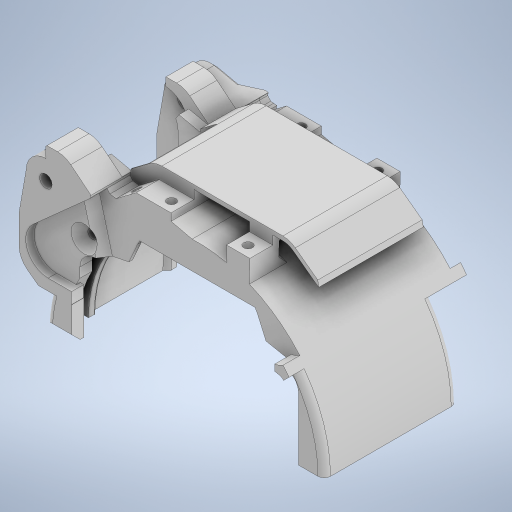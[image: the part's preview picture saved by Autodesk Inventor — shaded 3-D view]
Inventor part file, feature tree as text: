
AUTODESK INVENTOR PART (.ipt)
format: ipt  version: 2023.4 (Build 274418000, 418)  size: 2,114,560 bytes
history: native  units: mm
features: extrude x63, sketch x63, projected_geometry x51, chamfer x16, thicken_offset x6, fillet x4, plane x3
ambient origin geometry x8: Origin, YZ Plane, XZ Plane, XY Plane, X Axis, Y Axis, Z Axis, Center Point
bodies: Solid1 (feature_tree)
feature tree (206):
  extrude  "Extrusion1"  Depth=2.0mm
  extrude  "Extrusion2"  Depth=122.0mm
  extrude  "Extrusion3"  Depth=4.6mm TaperAngle=0.0deg
  extrude  "Extrusion4"  Depth=2.0mm TaperAngle=0.0deg
  extrude  "Extrusion5"  Depth=0.1mm
  thicken_offset  "Thicken1"
  thicken_offset  "Thicken2"
  extrude  "Extrusion6"  Depth=0.1mm
  extrude  "Extrusion7"  Depth=7.0mm TaperAngle=0.0deg
  extrude  "Extrusion8"  Depth=10.0mm TaperAngle=0.0deg
  extrude  "Extrusion9"  Depth=9.0mm TaperAngle=0.0deg
  extrude  "Extrusion10"  Depth=10.0mm TaperAngle=0.0deg
  extrude  "Extrusion11"  Depth=15.0mm TaperAngle=0.0deg
  extrude  "Extrusion12"  Depth=3.0mm
  sketch  "Sketch13"  dims[d40=4.0mm d41=0.0mm d42=12.0mm d43=0.0mm]
  plane  "Work Plane1"
  extrude  "Extrusion13"  Depth=12.0mm TaperAngle=0.0deg
  extrude  "Extrusion14"  Depth=7.0mm TaperAngle=0.0deg
  extrude  "Extrusion15"  Depth=5.0mm TaperAngle=0.0deg
  extrude  "Extrusion16"  Depth=1.0mm TaperAngle=0.0deg
  extrude  "Extrusion17"  Depth=4.0mm TaperAngle=0.0deg
  extrude  "Extrusion18"  Depth=10.0mm TaperAngle=0.0deg
  extrude  "Extrusion19"  Depth=15.0mm TaperAngle=0.0deg
  extrude  "Extrusion20"  Depth=10.0mm TaperAngle=0.0deg
  extrude  "Extrusion21"  Depth=1.3mm TaperAngle=45.0deg
  extrude  "Extrusion22"  Depth=10.0mm TaperAngle=0.0deg
  extrude  "Extrusion23"  Depth=3.0mm TaperAngle=0.0deg
  extrude  "Extrusion24"  Depth=2.0mm TaperAngle=45.0deg
  extrude  "Extrusion25"  Depth=3.0mm TaperAngle=0.0deg
  extrude  "Extrusion28"  Depth=10.0mm
  extrude  "Extrusion29"  Depth=4.0mm TaperAngle=45.0deg
  fillet  "Fillet2"  Radius=4.0mm
  extrude  "Extrusion30"  Depth=4.25mm
  extrude  "Extrusion31"  Depth=4.25mm
  extrude  "Extrusion32"  Depth=4.25mm
  chamfer  "Chamfer4"  Distance=9.0mm
  chamfer  "Chamfer5"  Distance=9.0mm
  chamfer  "Chamfer6"  Distance=6.0mm
  extrude  "Extrusion33"  Depth=6.0mm TaperAngle=0.0deg
  extrude  "Extrusion34"  Depth=4.0mm TaperAngle=0.0deg
  extrude  "Extrusion35"  Depth=30.0mm
  chamfer  "Chamfer7"  Distance=32.5mm
  extrude  "Extrusion36"  Depth=10.0mm
  extrude  "Extrusion37"  Depth=3.0mm TaperAngle=0.0deg
  extrude  "Extrusion38"  Depth=2.0mm TaperAngle=0.0deg
  chamfer  "Chamfer8"  Distance=4.0mm Angle=45.0deg
  chamfer  "Chamfer9"  Distance=4.0mm Angle=45.0deg
  chamfer  "Chamfer10"  Distance=0.5mm Angle=45.0deg
  extrude  "Extrusion39"  Depth=10.0mm
  extrude  "Extrusion40"  Depth=0.2mm
  extrude  "Extrusion41"  Depth=0.2mm
  extrude  "Extrusion42"  Depth=3.0mm TaperAngle=0.0deg
  extrude  "Extrusion43"  Depth=4.0mm TaperAngle=45.0deg
  extrude  "Extrusion44"  Depth=4.5mm
  extrude  "Extrusion45"  Depth=2.5mm
  extrude  "Extrusion46"  Depth=10.0mm TaperAngle=45.0deg
  extrude  "Extrusion47"  Depth=10.0mm TaperAngle=0.0deg
  plane  "Work Plane2"
  extrude  "Extrusion48"  Depth=10.0mm TaperAngle=0.0deg
  extrude  "Extrusion50"  Depth=4.0mm TaperAngle=45.0deg
  thicken_offset  "Thicken3"
  extrude  "Extrusion52"  Depth=3.0mm
  extrude  "Extrusion53"  TaperAngle=0.0deg  [1 undecoded]
  extrude  "Extrusion54"  Depth=2.0mm
  chamfer  "Chamfer13"  Distance=44.0mm
  chamfer  "Chamfer14"  Distance=4.0mm Angle=45.0deg
  chamfer  "Chamfer15"  Distance=44.0mm
  fillet  "Fillet3"  Radius=0.5mm
  thicken_offset  "Thicken4"
  thicken_offset  "Thicken5"
  thicken_offset  "Thicken6"
  extrude  "Extrusion55"  [1 undecoded]
  extrude  "Extrusion56"  [1 undecoded]
  extrude  "Extrusion57"  [1 undecoded]
  chamfer  "Chamfer16"  [1 undecoded]
  chamfer  "Chamfer18"  [1 undecoded]
  extrude  "Extrusion58"  [1 undecoded]
  extrude  "Extrusion59"  [1 undecoded]
  chamfer  "Chamfer19"  [1 undecoded]
  extrude  "Extrusion60"  [1 undecoded]
  extrude  "Extrusion61"  [1 undecoded]
  extrude  "Extrusion62"  [1 undecoded]
  extrude  "Extrusion63"  [1 undecoded]
  chamfer  "Chamfer21"  [1 undecoded]
  chamfer  "Chamfer22"  [1 undecoded]
  fillet  "Fillet4"  [1 undecoded]
  fillet  "Fillet5"  [1 undecoded]
  extrude  "Extrusion64"  [1 undecoded]
  extrude  "Extrusion65"  [1 undecoded]
  plane  "Work Plane3"
  extrude  "Extrusion66"  [1 undecoded]
  chamfer  "Chamfer23"  [1 undecoded]
  extrude  "Extrusion67"  [1 undecoded]
  sketch  "Sketch1"  dims[d0=125.0mm d1=2.0mm]
  sketch  "Sketch2"  dims[d2=4.6mm d3=0.0mm d4=122.0mm]
  sketch  "Sketch3"  dims[d5=42.8mm d6=0.0mm d7=4.6mm d8=0.0mm]
  projected_geometry  "Projected Loop1"
  sketch  "Sketch4"  dims[d10=2.0mm d11=0.0mm d12=2.0mm d13=0.0mm]
  sketch  "Sketch5"  dims[d14=0.1mm d15=0.1mm]
  projected_geometry  "Projected Loop2"
  projected_geometry  "Projected Loop3"
  sketch  "Sketch6"  dims[d16=0.1mm d17=0.1mm]
  projected_geometry  "Projected Loop4"
  sketch  "Sketch7"  dims[d18=0.0mm d19=0.0mm d20=7.0mm d21=0.0mm]
  projected_geometry  "Projected Loop5"
  sketch  "Sketch8"  dims[d22=0.0mm d23=0.0mm d24=10.0mm d25=0.0mm]
  projected_geometry  "Projected Loop6"
  projected_geometry  "Projected Loop7"
  sketch  "Sketch9"  dims[d26=9.0mm d27=0.0mm d28=9.0mm d29=0.0mm]
  projected_geometry  "Projected Loop8"
  sketch  "Sketch10"  dims[d30=10.0mm d31=0.0mm d32=10.0mm d33=0.0mm]
  sketch  "Sketch11"  dims[d34=15.0mm d35=0.0mm d36=15.0mm d37=0.0mm]
  projected_geometry  "Projected Loop9"
  sketch  "Sketch12"  dims[d38=3.0mm d39=3.0mm]
  projected_geometry  "Projected Loop10"
  sketch  "Sketch14"  dims[d44=3.0mm d45=0.0mm d46=7.0mm d47=0.0mm]
  projected_geometry  "Projected Loop11"
  projected_geometry  "Projected Loop12"
  sketch  "Sketch15"  dims[d48=2.0mm d49=0.0mm d50=5.0mm d51=0.0mm]
  sketch  "Sketch16"  dims[d52=5.0mm d53=0.0mm d54=1.0mm d55=0.0mm]
  projected_geometry  "Projected Loop13"
  sketch  "Sketch17"  dims[d56=4.0mm d57=0.0mm d58=4.0mm d59=0.0mm]
  sketch  "Sketch18"  dims[d74=10.0mm d75=0.0mm d76=3.9mm d77=0.0mm]
  projected_geometry  "Projected Loop14"
  sketch  "Sketch19"  dims[d78=3.0mm d79=15.0mm d80=0.0mm]
  sketch  "Sketch20"  dims[d81=15.0mm d82=0.0mm d83=10.0mm d84=0.0mm]
  projected_geometry  "Projected Loop15"
  sketch  "Sketch21"  dims[d85=4.0mm d86=2.0mm d87=45.0deg d88=1.3mm d89=2.0mm d90=45.0deg]
  projected_geometry  "Projected Loop16"
  sketch  "Sketch22"  dims[d91=3.0mm d92=2.0mm d93=45.0deg d94=10.0mm d95=0.0mm]
  projected_geometry  "Projected Loop17"
  projected_geometry  "Projected Loop18"
  projected_geometry  "Projected Loop19"
  projected_geometry  "Projected Loop20"
  projected_geometry  "Projected Loop21"
  projected_geometry  "Projected Loop22"
  projected_geometry  "Projected Loop23"
  projected_geometry  "Projected Loop24"
  projected_geometry  "Projected Loop25"
  projected_geometry  "Projected Loop26"
  sketch  "Sketch24"  dims[d96=2.0mm d97=3.0mm d98=0.0mm]
  projected_geometry  "Projected Loop28"
  sketch  "Sketch25"  dims[d99=3.0mm d100=0.0mm d101=2.0mm d102=2.0mm d103=45.0deg]
  sketch  "Sketch26"  dims[d104=6.0mm d105=3.0mm d106=0.0mm]
  sketch  "Sketch29"  dims[d107=10.0mm d108=0.0mm d109=11.2mm]
  projected_geometry  "Projected Loop31"
  sketch  "Sketch30"  dims[d110=6.0mm d111=0.0mm d112=4.0mm d113=2.0mm d114=45.0deg]
  projected_geometry  "Projected Loop32"
  sketch  "Sketch31"  dims[d115=2.0mm d116=2.0mm d117=45.0deg]
  sketch  "Sketch32"  dims[d118=1.0mm d119=2.0mm d120=45.0deg d121=4.0mm d122=0.0mm]
  sketch  "Sketch33"  dims[d123=4.25mm d124=4.25mm]
  sketch  "Sketch34"  dims[d125=4.25mm d126=4.25mm]
  sketch  "Sketch35"  dims[d127=9.0mm d128=0.0mm d129=4.25mm]
  sketch  "Sketch36"  dims[d130=4.25mm d131=9.0mm d132=0.0mm]
  projected_geometry  "Projected Loop33"
  sketch  "Sketch37"  dims[d133=4.25mm]
  projected_geometry  "Projected Loop34"
  sketch  "Sketch38"  dims[d134=4.25mm d135=9.0mm d136=0.0mm d137=6.0mm d138=0.0mm]
  projected_geometry  "Projected Loop35"
  sketch  "Sketch39"  dims[d139=6.0mm d140=0.0mm d141=6.0mm d142=0.0mm]
  sketch  "Sketch40"  dims[d143=9.0mm d144=0.0mm d145=4.0mm d146=0.0mm]
  projected_geometry  "Projected Loop36"
  sketch  "Sketch41"  dims[d147=-5.0mm d148=30.0mm d149=32.5mm d150=0.0mm]
  sketch  "Sketch42"  dims[d153=10.0mm d154=0.0mm d163=0.2mm]
  sketch  "Sketch43"  dims[d164=0.2mm d165=3.0mm d166=0.0mm]
  sketch  "Sketch44"  dims[d167=2.0mm d168=0.0mm d169=2.0mm d170=0.0mm d171=4.0mm d172=2.0mm d173=45.0deg d174=4.0mm d175=2.0mm d176=45.0deg d177=0.5mm d178=2.0mm d179=45.0deg]
  sketch  "Sketch45"  dims[d180=10.0mm d181=0.2mm]
  projected_geometry  "Projected Loop37"
  sketch  "Sketch46"  dims[d182=0.2mm d183=0.2mm d184=0.2mm]
  projected_geometry  "Projected Loop38"
  sketch  "Sketch47"  dims[d185=0.2mm d186=0.2mm]
  projected_geometry  "Projected Loop39"
  sketch  "Sketch48"  dims[d187=3.0mm d188=0.0mm d189=3.0mm d190=0.0mm]
  projected_geometry  "Projected Loop40"
  sketch  "Sketch49"  dims[d191=5.0mm d192=0.0mm d193=4.0mm d194=2.0mm d195=45.0deg]
  sketch  "Sketch51"  dims[d199=4.0mm d200=2.0mm d201=45.0deg d202=4.5mm]
  projected_geometry  "Projected Loop41"
  sketch  "Sketch53"  dims[d203=0.0mm d204=0.0mm d205=2.5mm]
  projected_geometry  "Projected Loop42"
  sketch  "Sketch54"  dims[d206=10.0mm d207=0.0mm d208=4.0mm d209=2.0mm d210=45.0deg]
  projected_geometry  "Projected Loop43"
  projected_geometry  "Projected Loop44"
  sketch  "Sketch55"  dims[d211=10.0mm d212=0.0mm d216=5.0mm d217=0.0mm]
  projected_geometry  "Projected Loop45"
  projected_geometry  "Projected Loop46"
  sketch  "Sketch56"  dims[d218=5.0mm d219=0.0mm d220=10.0mm d221=0.0mm]
  projected_geometry  "Projected Loop47"
  sketch  "Sketch57"  dims[d222=4.0mm d223=2.0mm d224=45.0deg d225=4.0mm d226=2.0mm d227=45.0deg]
  projected_geometry  "Projected Loop48"
  sketch  "Sketch58"  dims[d228=3.0mm d229=3.0mm]
  projected_geometry  "Projected Loop49"
  sketch  "Sketch59"  dims[d230=6.108652mm d231=0.0mm d232=0.0mm]
  sketch  "Sketch60"  dims[d233=0.0mm d234=0.0mm d235=2.0mm]
  sketch  "Sketch61"  dims[d236=-3.0mm d237=44.0mm d238=0.0mm d239=4.0mm d240=2.0mm d241=45.0deg]
  sketch  "Sketch62"  dims[d242=45.0deg d243=44.0mm d244=0.0mm d9=0.5mm]
  projected_geometry  "Projected Loop50"
  sketch  "Sketch63"
  sketch  "Sketch64"
  projected_geometry  "Projected Loop51"
  projected_geometry  "Projected Loop52"
  sketch  "Sketch65"
  projected_geometry  "Projected Loop53"
  sketch  "Sketch66"
  projected_geometry  "Projected Loop54"
  sketch  "Sketch67"
  sketch  "Sketch68"
note: 22 required parameter values undecoded (feature->parameter linkage not recoverable at this tier; creation-order binding heuristic only, values carry confidence <= 0.55)
